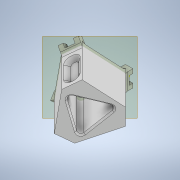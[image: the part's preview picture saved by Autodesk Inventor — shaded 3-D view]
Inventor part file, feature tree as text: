
AUTODESK INVENTOR PART (.ipt)
format: ipt  version: 2020 (Build 240168000, 168)  size: 359,424 bytes
history: native  units: mm
features: sketch x7, extrude x6, fillet x4, projected_geometry x4, other x4, thicken_offset x3, chamfer x3, plane x2, pattern_circular x2, reference x2
ambient origin geometry x8: Origin, YZ Plane, XZ Plane, XY Plane, X Axis, Y Axis, Z Axis, Center Point
bodies: Solid1 (feature_tree)
feature tree (37):
  extrude  "Extrusion1"  Depth=10.0mm
  extrude  "Extrusion2"  Depth=10.0mm
  thicken_offset  "Thicken1"
  thicken_offset  "Thicken2"
  plane  "Work Plane1"
  extrude  "Extrusion3"  Depth=10.0mm
  pattern_circular  "Circular Pattern1"  [2 undecoded]
  plane  "Work Plane2"
  extrude  "Extrusion4"  Depth=3.0mm
  fillet  "Fillet1"  Radius=3.0mm
  fillet  "Fillet2"  Radius=5.0mm
  fillet  "Fillet3"  Radius=30.0mm
  extrude  "Extrusion5"  Depth=5.0mm TaperAngle=0.0deg
  sketch  "Sketch6"  dims[d10=3.0mm]
  fillet  "Fillet4"  Radius=2.0mm
  chamfer  "Chamfer1"  Distance=4.0mm
  extrude  "Extrusion9"  Depth=3.0mm
  chamfer  "Chamfer2"  Distance=55.0mm
  pattern_circular  "Circular Pattern4"  [2 undecoded]
  chamfer  "Chamfer3"  Distance=2.0mm Angle=45.0deg
  thicken_offset  "Thicken6"
  sketch  "Sketch1"  dims[d0=10.0mm d1=16.0mm]
  reference  "Reference1"
  sketch  "Sketch2"  dims[d2=5.0mm d3=0.0mm d4=10.0mm]
  projected_geometry  "Projected Loop1"
  sketch  "Sketch3"  dims[d5=2.5mm d6=10.0mm]
  reference  "Reference2"
  sketch  "Sketch4"  dims[d7=2.5mm]
  sketch  "Sketch5"  dims[d8=5.0mm d9=0.0mm]
  projected_geometry  "Projected Loop2"
  projected_geometry  "Projected Loop3"
  sketch  "Sketch9"  dims[d11=3.0mm d12=3.0mm d13=3.0mm d14=3.0mm d15=5.0mm d16=0.0mm d17=30.0mm d18=360.0deg d20=5.0mm d21=0.0mm d22=2.0mm d23=4.0mm d24=3.0mm d25=55.0mm d26=0.0mm d27=8.0mm d38=2.0mm d39=2.0mm d40=45.0deg d43=12.0mm d44=8.0mm d45=5.0mm d46=0.0mm d47=5.0mm d48=2.0mm d49=45.0deg d50=30.0mm d51=360.0deg d53=5.0mm d54=2.0mm d55=45.0deg d70=10.0mm d71=10.0mm d28=0.872665mm d29=0.5mm d30=0.872665mm d56=0.5mm d57=0.872665mm d58=0.5mm d59=0.872665mm]
  projected_geometry  "Projected Loop5"
  parser-record x1  (decoder bookkeeping rows leaked as tree rows — omitted from the tree; the rows remain in map.json)
  other  "delta_1.iam"
  other  "arm_holder_2:2"
  other  "arm_holder_1:1"
note: 4 required parameter values undecoded (feature->parameter linkage not recoverable at this tier; creation-order binding heuristic only, values carry confidence <= 0.55)
note: 1 file-system path scrubbed to <path> (originals preserved in map.json)
